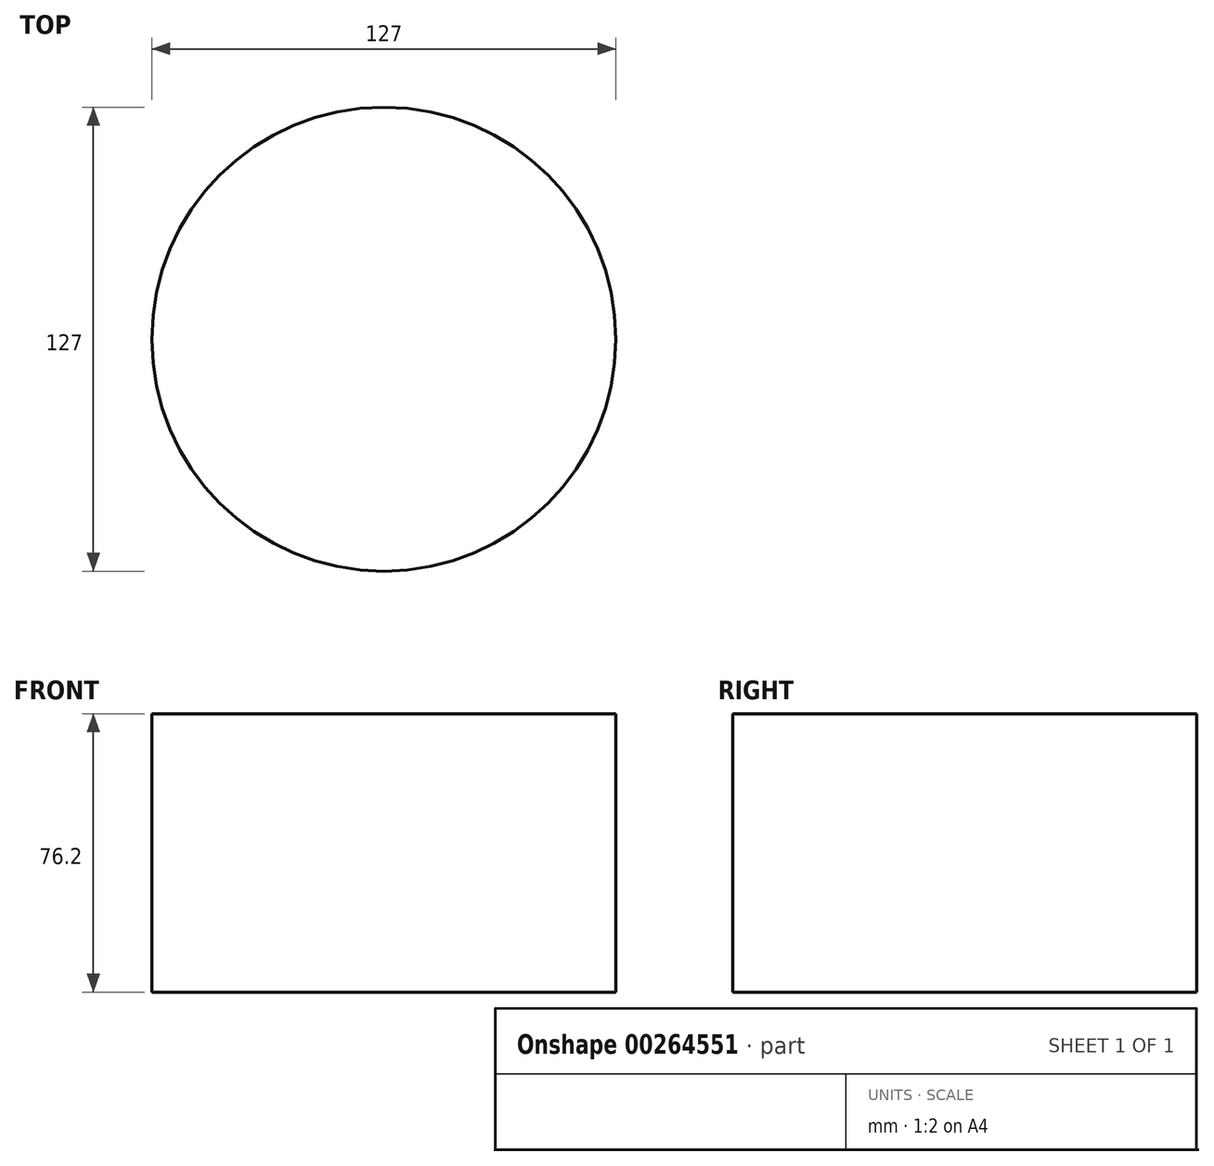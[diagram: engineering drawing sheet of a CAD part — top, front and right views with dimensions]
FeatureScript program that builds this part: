
annotation { "Feature Type Name" : "Feature", "Feature Type Description" : "" }
export const myFeature = defineFeature(function(context is Context, id is Id, definition is map)
    precondition{}
    {
        {
            var Q0;
            Q0=qCreatedBy(makeId("Top.planeOp"),FACE);
            var sketch = newSketch(context, id + "F0", { "sketchPlane" : qUnion([Q0])});
            skCircle(sketch, "E0", {"center": v(0, 0) * mm, "radius": 63.5 * mm});
            skSolve(sketch);
        }
        {
            var Q0;
            Q0 = qSketchRegion(id + "F0", true);
            extrude(context, id + "F1", {"entities" : qUnion([Q0]), "depth" : 76.2 * mm});
        }
    });
